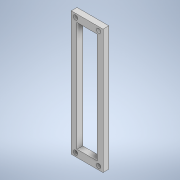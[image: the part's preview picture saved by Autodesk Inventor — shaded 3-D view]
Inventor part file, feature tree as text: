
AUTODESK INVENTOR PART (.ipt)
format: ipt  version: 2020.2 (Build 242310000, 310)  size: 124,416 bytes
history: native  units: mm
features: extrude x1, sketch x1
ambient origin geometry x8: Origin, YZ Plane, XZ Plane, XY Plane, X Axis, Y Axis, Z Axis, Center Point
bodies: Solid1 (feature_tree)
feature tree (2):
  extrude  "Extrusion1"  Depth=86.0mm
  sketch  "Sketch1"  dims[d0=22.0mm d1=86.0mm d2=3.0mm d3=3.0mm d4=3.0mm d5=3.0mm d6=3.0mm d7=2.5mm d8=3.0mm d9=2.5mm d10=2.5mm d11=3.0mm d12=3.0mm d13=2.5mm d14=14.0mm d15=76.0mm d16=4.0mm d17=0.0mm]
